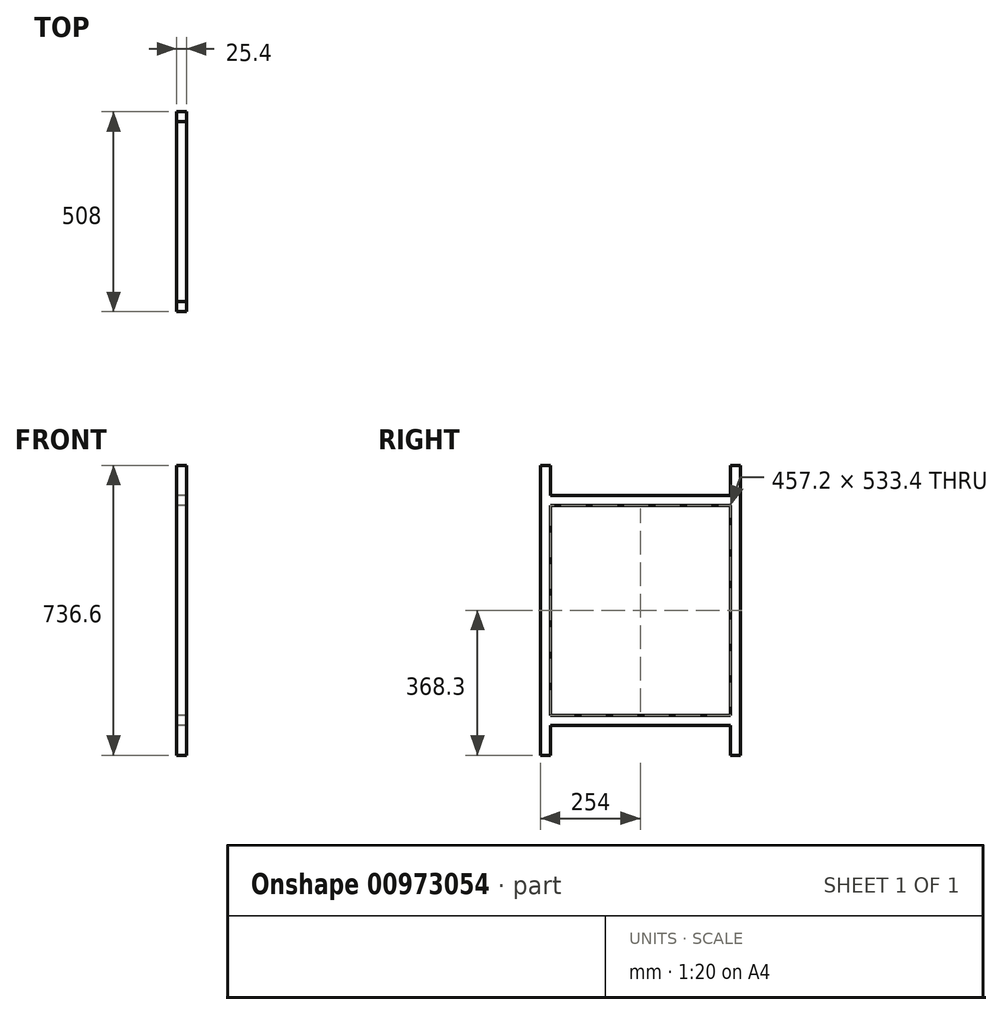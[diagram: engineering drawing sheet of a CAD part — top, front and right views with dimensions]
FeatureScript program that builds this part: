
annotation { "Feature Type Name" : "Feature", "Feature Type Description" : "" }
export const myFeature = defineFeature(function(context is Context, id is Id, definition is map)
    precondition{}
    {
        {
            var Q0;
            Q0=qCreatedBy(makeId("Right.planeOp"),FACE);
            var sketch = newSketch(context, id + "F0", { "sketchPlane" : qUnion([Q0])});
            skLineSegment(sketch, "E0.bottom", {"start": v(0, 0) * mm, "end": v(25.4, 0) * mm});
            skLineSegment(sketch, "E0.top", {"start": v(0, 736.6) * mm, "end": v(25.4, 736.6) * mm});
            skLineSegment(sketch, "E0.left", {"start": v(0, 0) * mm, "end": v(0, 736.6) * mm});
            skLineSegment(sketch, "E0.right", {"start": v(25.4, 0) * mm, "end": v(25.4, 76.2) * mm});
            skLineSegment(sketch, "E1.bottom", {"start": v(25.4, 101.6) * mm, "end": v(482.6, 101.6) * mm});
            skLineSegment(sketch, "E1.top", {"start": v(25.4, 76.2) * mm, "end": v(482.6, 76.2) * mm});
            skLineSegment(sketch, "E2.bottom", {"start": v(482.6, 736.6) * mm, "end": v(508, 736.6) * mm});
            skLineSegment(sketch, "E2.top", {"start": v(482.6, 0) * mm, "end": v(508, 0) * mm});
            skLineSegment(sketch, "E2.left", {"start": v(482.6, 736.6) * mm, "end": v(482.6, 660.4) * mm});
            skLineSegment(sketch, "E2.right", {"start": v(508, 736.6) * mm, "end": v(508, 0) * mm});
            skLineSegment(sketch, "E3.bottom", {"start": v(25.4, 660.4) * mm, "end": v(482.6, 660.4) * mm});
            skLineSegment(sketch, "E3.top", {"start": v(25.4, 635) * mm, "end": v(482.6, 635) * mm});
            skLineSegment(sketch, "E4.trimOffspring", {"start": v(25.4, 660.4) * mm, "end": v(25.4, 736.6) * mm});
            skLineSegment(sketch, "E5.trimOffspring", {"start": v(482.6, 635) * mm, "end": v(482.6, 101.6) * mm});
            skLineSegment(sketch, "E6.trimOffspring", {"start": v(482.6, 76.2) * mm, "end": v(482.6, 0) * mm});
            skLineSegment(sketch, "E7.trimOffspring", {"start": v(25.4, 101.6) * mm, "end": v(25.4, 635) * mm});
            skSolve(sketch);
        }
        {
            var Q0;
            Q0=makeQuery(id+"F0.imprint","IMPRINT",FACE,{"disambiguationData":[TD([[makeQuery(id+"F0.imprint","IMPRINT",EDGE,{"derivedFrom":sQuery(id+"F0.wireOp",EDGE,"E0.bottom")}),1.0]])]});
            extrude(context, id + "F1", {"entities" : qUnion([Q0]), "depth" : 25.4 * mm, "offsetDistance" : 25.4 * mm});
        }
    });
